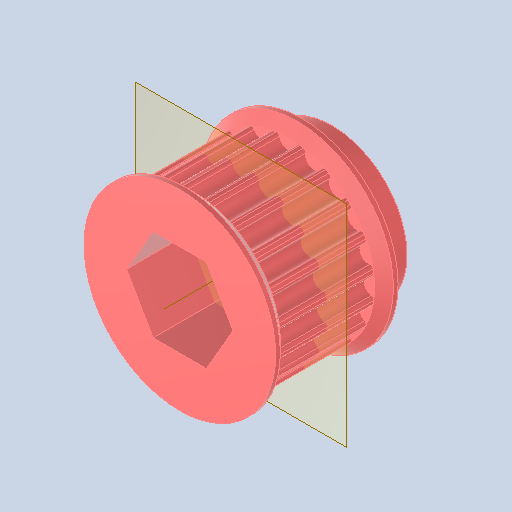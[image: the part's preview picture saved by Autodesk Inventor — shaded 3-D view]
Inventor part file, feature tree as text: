
AUTODESK INVENTOR PART (.ipt)
format: ipt  version: 2022.3 (Build 263350000, 350)  size: 316,928 bytes
history: native  units: in
note: dims shown in document units (in); Inventor stores cm internally (conversion verified against a paired STEP export)
features: extrude x7, sketch x7, mirror x2, chamfer x2, other x1, fillet x1, pattern_circular x1, projected_geometry x1
ambient origin geometry x8: Origin, YZ Plane, XZ Plane, XY Plane, X Axis, Y Axis, Z Axis, Center Point
bodies: Solid1 (feature_tree)
feature tree (22):
  other  "Hex Bore"
  extrude  "HTD Base"  Depth=0.3937in TaperAngle=0.0deg
  extrude  "HTD Flange"  Depth=0.0591in
  mirror  "HTD Flanges"
  chamfer  "HTD Flange Chamfer"  Distance=0.0787in Angle=45.0deg
  extrude  "GT2 Base"  TaperAngle=0.0deg  [1 undecoded]
  extrude  "GT2 Base Tooth"  TaperAngle=0.0deg  [1 undecoded]
  fillet  "GT2 Base Tooth pt. 2"  Radius=0.7219in
  pattern_circular  "GT2 Teeth"  [2 undecoded]
  extrude  "GT2 Flange"  Depth=0.125in
  mirror  "GT2 Flanges"
  chamfer  "GT2 Flange Chamfer"  Distance=0.0075in
  extrude  "Circle Bore"  TaperAngle=0.0deg  [1 undecoded]
  extrude  "Extrusion9"  Depth=0.0118in
  sketch  "Sketch1"  dims[d0=1.2082in d1=0.3937in d2=0.0in]
  sketch  "Sketch4"  dims[d12=0.0394in d13=0.0591in]
  sketch  "Sketch5"  dims[d14=0.0in]
  sketch  "Sketch6"  dims[d15=0.0394in d16=0.0787in d17=45.0deg]
  sketch  "Sketch7"  dims[d18=0.385in d19=0.0in d20=0.0in]
  sketch  "Sketch8"  dims[d21=0.385in d22=0.0in d23=0.0in d24=0.7219in]
  sketch  "Sketch9"  dims[d25=0.3937in d26=0.0in d27=0.0727in d28=0.0075in d29=0.0in d30=0.0in d31=0.0118in d32=7.874in d33=360.0deg d35=0.0394in d36=0.0591in d37=0.0in d38=0.0394in d39=0.0787in d40=45.0deg d41=0.625in d42=0.125in d43=0.0in]
  projected_geometry  "Projected Loop1"
note: 5 required parameter values undecoded (feature->parameter linkage not recoverable at this tier; creation-order binding heuristic only, values carry confidence <= 0.55)
